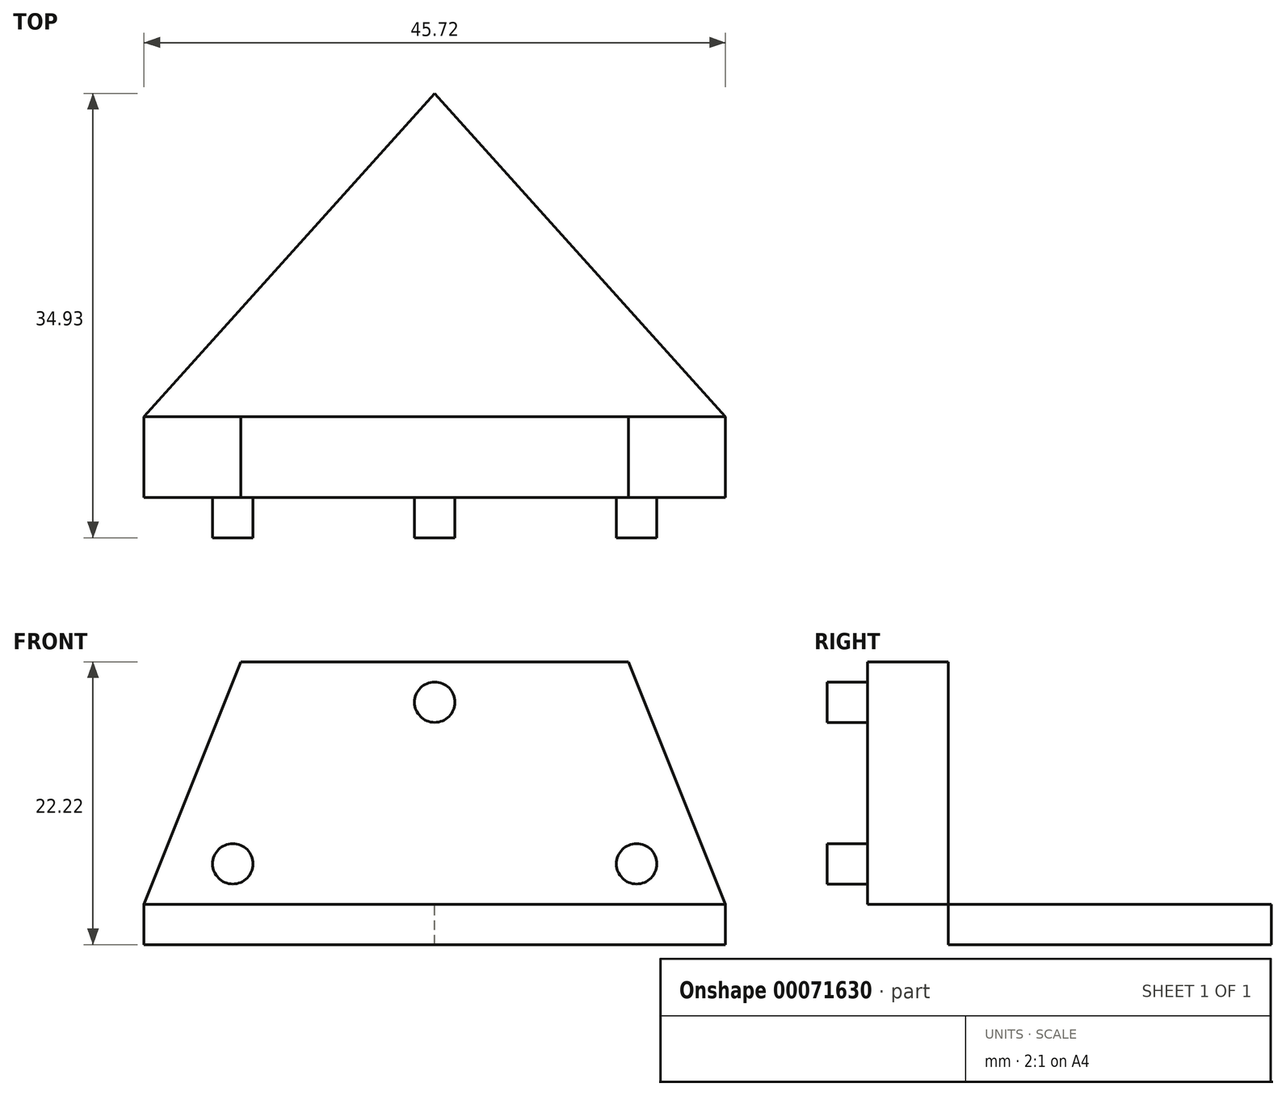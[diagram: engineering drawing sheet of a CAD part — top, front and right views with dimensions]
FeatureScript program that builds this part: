
annotation { "Feature Type Name" : "Feature", "Feature Type Description" : "" }
export const myFeature = defineFeature(function(context is Context, id is Id, definition is map)
    precondition{}
    {
        {
            var Q0;
            Q0=qCreatedBy(makeId("Front.planeOp"),FACE);
            var sketch = newSketch(context, id + "F0", { "sketchPlane" : qUnion([Q0])});
            skLineSegment(sketch, "E0", {"start": v(-65.44, 6.31) * mm, "end": v(-19.72, 6.31) * mm});
            skLineSegment(sketch, "E1", {"start": v(-42.58, 25.36) * mm, "end": v(-27.34, 25.36) * mm});
            skLineSegment(sketch, "E2", {"start": v(-42.58, 25.36) * mm, "end": v(-57.82, 25.36) * mm});
            skLineSegment(sketch, "E3", {"start": v(-57.82, 25.36) * mm, "end": v(-65.44, 6.31) * mm});
            skLineSegment(sketch, "E4", {"start": v(-27.34, 25.36) * mm, "end": v(-19.72, 6.31) * mm});
            skSolve(sketch);
        }
        {
            var Q0;
            Q0 = qSketchRegion(id + "F0", true);
            extrude(context, id + "F1", {"entities" : qUnion([Q0]), "depth" : 6.35 * mm});
        }
        {
            var Q0;
            Q0=makeQuery(id+"F1.opExtrude","CAP_FACE",FACE,{"disambiguationData":[OSD([sQuery(id+"F0.wireOp",EDGE,"E0"),sQuery(id+"F0.wireOp",EDGE,"E1"),sQuery(id+"F0.wireOp",EDGE,"E2"),sQuery(id+"F0.wireOp",EDGE,"E3"),sQuery(id+"F0.wireOp",EDGE,"E4")])],"isStart":false});
            var sketch = newSketch(context, id + "F2", { "sketchPlane" : qUnion([Q0])});
            skCircle(sketch, "E5", {"center": v(-58.45, 9.49) * mm, "radius": 1.59 * mm});
            skCircle(sketch, "E6", {"center": v(-26.7, 9.49) * mm, "radius": 1.59 * mm});
            skCircle(sketch, "E7", {"center": v(-42.58, 22.19) * mm, "radius": 1.59 * mm});
            skSolve(sketch);
        }
        {
            var Q0;
            Q0 = qSketchRegion(id + "F2", true);
            extrude(context, id + "F3", {"entities" : qUnion([Q0]), "operationType" : NewBodyOperationType.ADD, "depth" : 3.17 * mm});
        }
        {
            var Q0;
            Q0=makeQuery(id+"F1.opExtrude","SWEPT_FACE",FACE,{"disambiguationData":[OSD([sQuery(id+"F0.wireOp",EDGE,"E0")])]});
            var sketch = newSketch(context, id + "F4", { "sketchPlane" : qUnion([Q0])});
            skLineSegment(sketch, "E8", {"start": v(-42.58, 0) * mm, "end": v(-42.58, -25.4) * mm});
            skLineSegment(sketch, "E9", {"start": v(-42.58, -25.4) * mm, "end": v(-19.72, 0) * mm});
            skLineSegment(sketch, "E10", {"start": v(-42.58, -25.4) * mm, "end": v(-65.44, 0) * mm});
            skLineSegment(sketch, "E11", {"start": v(-19.72, 0) * mm, "end": v(-65.44, 0) * mm});
            skSolve(sketch);
        }
        {
            var Q0;
            Q0 = qSketchRegion(id + "F4", true);
            extrude(context, id + "F5", {"entities" : qUnion([Q0]), "operationType" : NewBodyOperationType.ADD, "depth" : 3.17 * mm});
        }
        {
            var Q0;
            Q0 = qSketchRegion(id + "F4", true);
            extrude(context, id + "F6", {"entities" : qUnion([Q0]), "operationType" : NewBodyOperationType.REMOVE, "oppositeDirection" : true, "depth" : 3.17 * mm});
        }
    });
